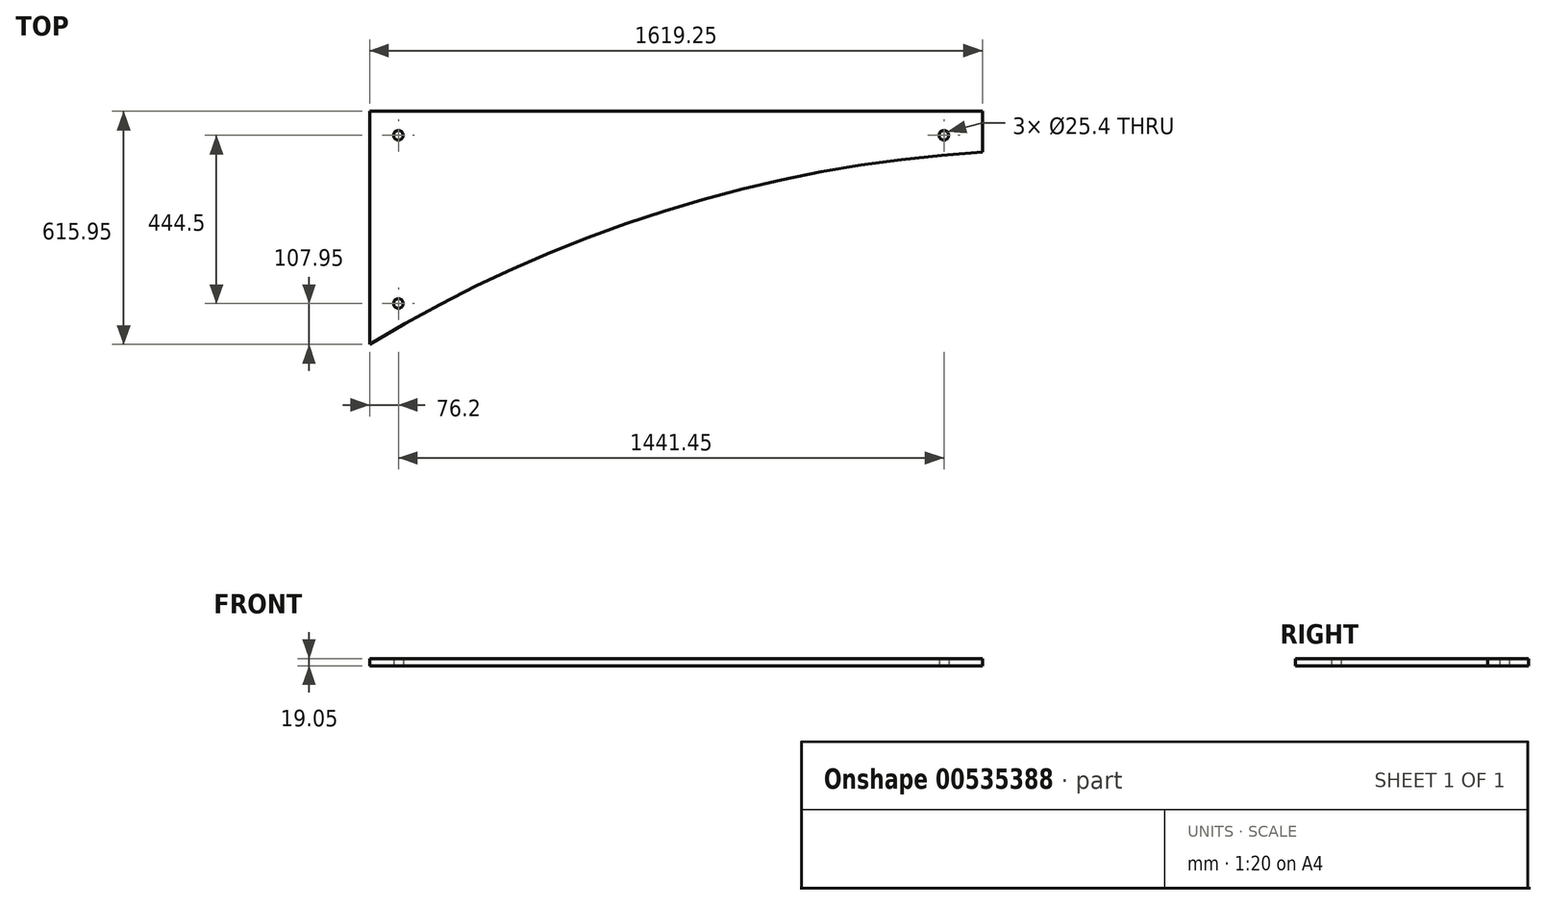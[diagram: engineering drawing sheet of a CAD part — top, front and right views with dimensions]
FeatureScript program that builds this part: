
annotation { "Feature Type Name" : "Feature", "Feature Type Description" : "" }
export const myFeature = defineFeature(function(context is Context, id is Id, definition is map)
    precondition{}
    {
        {
            var Q0;
            Q0=qCreatedBy(makeId("Top.planeOp"),FACE);
            var sketch = newSketch(context, id + "F0", { "sketchPlane" : qUnion([Q0])});
            skLineSegment(sketch, "E0", {"start": v(0, 0) * mm, "end": v(0, 615.95) * mm});
            skLineSegment(sketch, "E1", {"start": v(0, 615.95) * mm, "end": v(0, 615.95) * mm});
            skLineSegment(sketch, "E2", {"start": v(0, 615.95) * mm, "end": v(-1619.25, 615.95) * mm, "construction": true});
            skLineSegment(sketch, "E3", {"start": v(-809.62, 615.95) * mm, "end": v(-809.62, 361.95) * mm, "construction": true});
            skLineSegment(sketch, "E4", {"start": v(-1619.25, 615.95) * mm, "end": v(-1619.25, 508) * mm, "construction": true});
            skArc(sketch, "E5", {"start": v(0, 0) * mm, "mid": v(-778.75, 352.42) * mm, "end": v(-1619.25, 508) * mm, "construction": true});
            skLineSegment(sketch, "E6.0", {"start": v(-76.2, 552.45) * mm, "end": v(-1590.67, 552.45) * mm, "construction": true});
            skCircle(sketch, "E7", {"center": v(-76.2, 552.45) * mm, "radius": 12.7 * mm, "construction": true});
            skLineSegment(sketch, "E8.0", {"start": v(0, 107.95) * mm, "end": v(-76.2, 107.95) * mm, "construction": true});
            skLineSegment(sketch, "E9.trimOffspring", {"start": v(-76.2, 107.95) * mm, "end": v(-76.2, 552.45) * mm, "construction": true});
            skCircle(sketch, "E10", {"center": v(-76.2, 107.95) * mm, "radius": 12.7 * mm, "construction": true});
            skLineSegment(sketch, "E11.0", {"start": v(-1517.65, 552.45) * mm, "end": v(-1517.65, 615.95) * mm, "construction": true});
            skCircle(sketch, "E12", {"center": v(-1517.65, 552.45) * mm, "radius": 12.7 * mm, "construction": true});
            skArc(sketch, "E13.MirrorCS", {"start": v(0, 0) * mm, "mid": v(778.75, 352.42) * mm, "end": v(1619.25, 508) * mm});
            skLineSegment(sketch, "E14.MirrorCS", {"start": v(0, 615.95) * mm, "end": v(1619.25, 615.95) * mm});
            skCircle(sketch, "E15.MirrorC", {"center": v(76.2, 107.95) * mm, "radius": 12.7 * mm});
            skCircle(sketch, "E16.MirrorC", {"center": v(76.2, 552.45) * mm, "radius": 12.7 * mm});
            skLineSegment(sketch, "E17.MirrorCS", {"start": v(809.62, 615.95) * mm, "end": v(809.62, 361.95) * mm, "construction": true});
            skCircle(sketch, "E18.MirrorC", {"center": v(1517.65, 552.45) * mm, "radius": 12.7 * mm});
            skLineSegment(sketch, "E19.MirrorCS", {"start": v(1619.25, 615.95) * mm, "end": v(1619.25, 508) * mm});
            skSolve(sketch);
        }
        {
            var Q0;
            Q0=makeQuery(id+"F0.imprint","IMPRINT",FACE,{"disambiguationData":[TD([[makeQuery(id+"F0.imprint","IMPRINT",EDGE,{"derivedFrom":sQuery(id+"F0.wireOp",EDGE,"E0")}),-1.0]])]});
            extrude(context, id + "F1", {"entities" : qUnion([Q0]), "depth" : 19.05 * mm, "offsetDistance" : 25.4 * mm});
        }
    });
